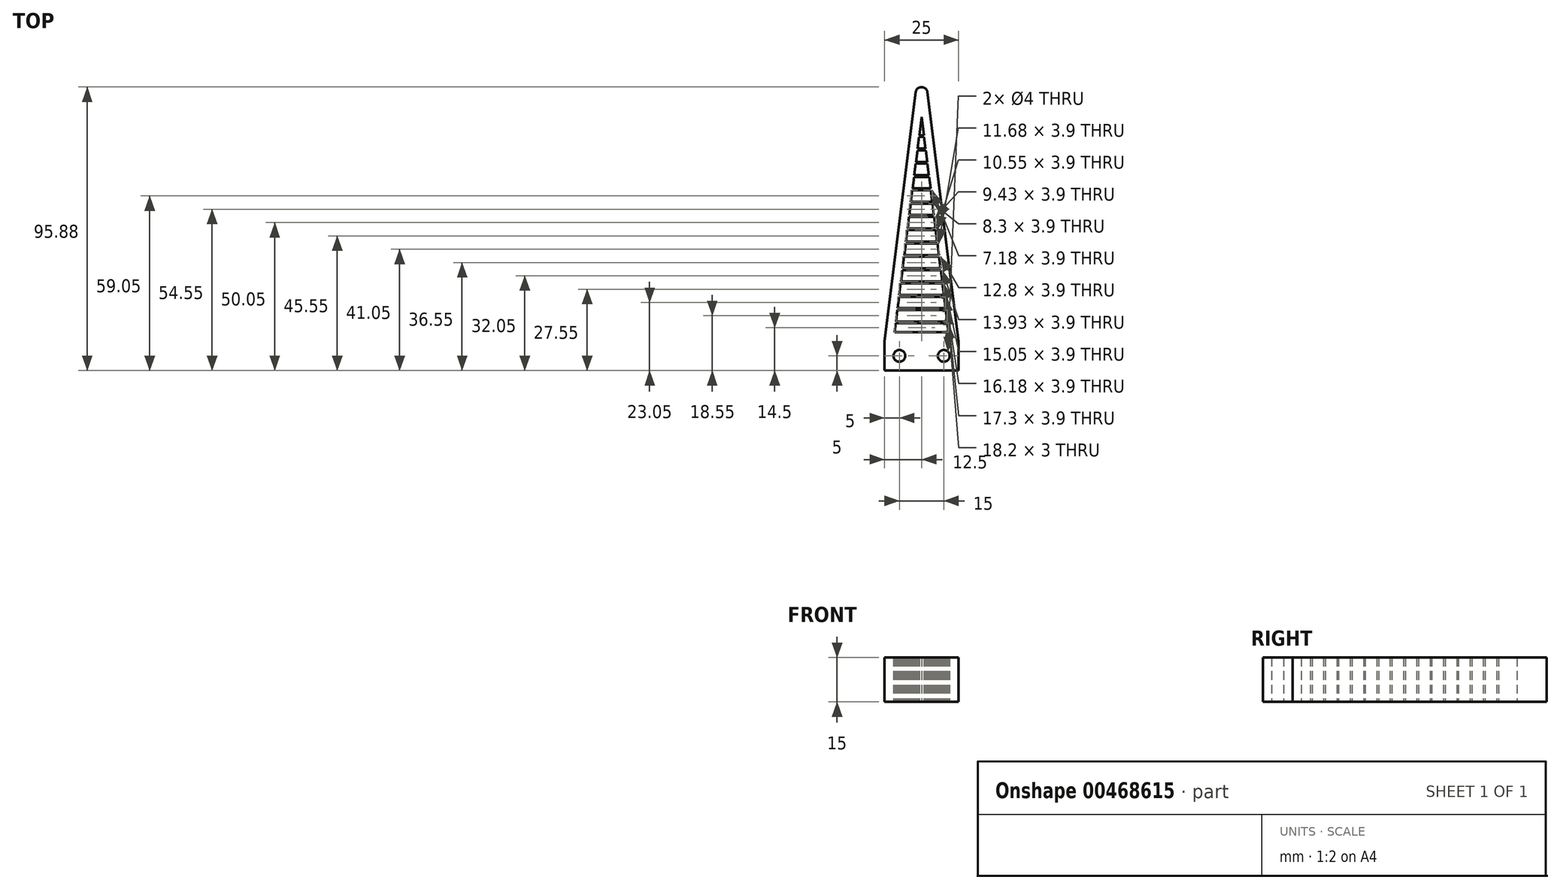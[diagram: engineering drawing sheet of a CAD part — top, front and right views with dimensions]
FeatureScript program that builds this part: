
annotation { "Feature Type Name" : "Feature", "Feature Type Description" : "" }
export const myFeature = defineFeature(function(context is Context, id is Id, definition is map)
    precondition{}
    {
        {
            var Q0;
            Q0=qCreatedBy(makeId("Top.planeOp"),FACE);
            var sketch = newSketch(context, id + "F0", { "sketchPlane" : qUnion([Q0])});
            skLineSegment(sketch, "E0", {"start": v(0, 0) * mm, "end": v(25, 0) * mm});
            skLineSegment(sketch, "E1", {"start": v(25, 0) * mm, "end": v(12.5, 100) * mm});
            skPoint(sketch, "E1.endSnap0", {"position": v(12.5, 0) * mm});
            skLineSegment(sketch, "E2", {"start": v(12.5, 100) * mm, "end": v(0, 0) * mm});
            skLineSegment(sketch, "E3.0", {"start": v(12.5, 75.81) * mm, "end": v(3.4, 3) * mm});
            skLineSegment(sketch, "E3.1", {"start": v(21.6, 3) * mm, "end": v(12.5, 75.81) * mm});
            skLineSegment(sketch, "E3.2", {"start": v(3.4, 3) * mm, "end": v(21.6, 3) * mm});
            skLineSegment(sketch, "E4", {"start": v(0, 0) * mm, "end": v(0, 100) * mm, "construction": true});
            skLineSegment(sketch, "E5", {"start": v(0, 100) * mm, "end": v(25, 100) * mm, "construction": true});
            skLineSegment(sketch, "E6", {"start": v(25, 100) * mm, "end": v(25, 0) * mm, "construction": true});
            skLineSegment(sketch, "E7.top", {"start": v(0, -10) * mm, "end": v(25, -10) * mm});
            skLineSegment(sketch, "E7.left", {"start": v(0, 0) * mm, "end": v(0, -10) * mm});
            skLineSegment(sketch, "E7.right", {"start": v(25, 0) * mm, "end": v(25, -10) * mm});
            skCircle(sketch, "E8", {"center": v(20, -5) * mm, "radius": 2 * mm});
            skPoint(sketch, "E8.centerSnap0", {"position": v(25, -5) * mm});
            skCircle(sketch, "E9", {"center": v(5, -5) * mm, "radius": 2 * mm});
            skPoint(sketch, "E9.centerSnap0", {"position": v(0, -5) * mm});
            skLineSegment(sketch, "E10", {"start": v(3.77, 6) * mm, "end": v(21.23, 6) * mm});
            skLineSegment(sketch, "E11", {"start": v(3.85, 6.6) * mm, "end": v(21.15, 6.6) * mm});
            skLineSegment(sketch, "E12.0.1.0", {"start": v(3.77, 10.5) * mm, "end": v(21.23, 10.5) * mm});
            skLineSegment(sketch, "E12.0.1.1", {"start": v(3.85, 11.1) * mm, "end": v(21.15, 11.1) * mm});
            skLineSegment(sketch, "E12.0.2.0", {"start": v(3.77, 15) * mm, "end": v(21.23, 15) * mm});
            skLineSegment(sketch, "E12.0.2.1", {"start": v(3.85, 15.6) * mm, "end": v(21.15, 15.6) * mm});
            skLineSegment(sketch, "E12.0.3.0", {"start": v(3.77, 19.5) * mm, "end": v(21.23, 19.5) * mm});
            skLineSegment(sketch, "E12.0.3.1", {"start": v(3.85, 20.1) * mm, "end": v(21.15, 20.1) * mm});
            skLineSegment(sketch, "E12.0.4.0", {"start": v(3.77, 24) * mm, "end": v(21.23, 24) * mm});
            skLineSegment(sketch, "E12.0.4.1", {"start": v(3.85, 24.6) * mm, "end": v(21.15, 24.6) * mm});
            skLineSegment(sketch, "E12.0.5.0", {"start": v(3.77, 28.5) * mm, "end": v(21.23, 28.5) * mm});
            skLineSegment(sketch, "E12.0.5.1", {"start": v(3.85, 29.1) * mm, "end": v(21.15, 29.1) * mm});
            skLineSegment(sketch, "E12.0.6.0", {"start": v(3.77, 33) * mm, "end": v(21.23, 33) * mm});
            skLineSegment(sketch, "E12.0.6.1", {"start": v(3.85, 33.6) * mm, "end": v(21.15, 33.6) * mm});
            skLineSegment(sketch, "E12.0.7.0", {"start": v(3.77, 37.5) * mm, "end": v(21.23, 37.5) * mm});
            skLineSegment(sketch, "E12.0.7.1", {"start": v(3.85, 38.1) * mm, "end": v(21.15, 38.1) * mm});
            skLineSegment(sketch, "E12.0.8.0", {"start": v(3.77, 42) * mm, "end": v(21.23, 42) * mm});
            skLineSegment(sketch, "E12.0.8.1", {"start": v(3.85, 42.6) * mm, "end": v(21.15, 42.6) * mm});
            skLineSegment(sketch, "E12.0.9.0", {"start": v(3.77, 46.5) * mm, "end": v(21.23, 46.5) * mm});
            skLineSegment(sketch, "E12.0.9.1", {"start": v(3.85, 47.1) * mm, "end": v(21.15, 47.1) * mm});
            skLineSegment(sketch, "E12.0.10.0", {"start": v(3.77, 51) * mm, "end": v(21.23, 51) * mm});
            skLineSegment(sketch, "E12.0.10.1", {"start": v(3.85, 51.6) * mm, "end": v(21.15, 51.6) * mm});
            skLineSegment(sketch, "E12.direction1", {"start": v(3.77, 6) * mm, "end": v(35.36, 6) * mm, "construction": true});
            skLineSegment(sketch, "E12.direction2", {"start": v(3.77, 6) * mm, "end": v(3.77, 10.5) * mm, "construction": true});
            skLineSegment(sketch, "E13.0.0.11", {"start": v(3.77, 55.5) * mm, "end": v(21.23, 55.5) * mm});
            skLineSegment(sketch, "E13.3.0.11", {"start": v(3.85, 56.1) * mm, "end": v(21.15, 56.1) * mm});
            skLineSegment(sketch, "E13.0.0.12", {"start": v(3.77, 60) * mm, "end": v(21.23, 60) * mm});
            skLineSegment(sketch, "E13.3.0.12", {"start": v(3.85, 60.6) * mm, "end": v(21.15, 60.6) * mm});
            skLineSegment(sketch, "E13.0.0.13", {"start": v(3.77, 64.5) * mm, "end": v(21.23, 64.5) * mm});
            skLineSegment(sketch, "E13.3.0.13", {"start": v(3.85, 65.1) * mm, "end": v(21.15, 65.1) * mm});
            skLineSegment(sketch, "E13.0.0.14", {"start": v(3.77, 69) * mm, "end": v(21.23, 69) * mm});
            skLineSegment(sketch, "E13.3.0.14", {"start": v(3.85, 69.6) * mm, "end": v(21.15, 69.6) * mm});
            skSolve(sketch);
        }
        {
            var Q0;
            {var subQ0=sQuery(id+"F0.wireOp",EDGE,"E12.0.5.0");var subQ1=sQuery(id+"F0.wireOp",EDGE,"E1");var subQ2=makeQuery(id+"F0.imprint","INTERSECT",VERTEX,{"derivedFrom":[subQ1,subQ0]});Q0=makeQuery(id+"F0.imprint","IMPRINT",FACE,{"disambiguationData":[TD([[makeQuery(id+"F0.imprint","IMPRINT",EDGE,{"disambiguationData":[TD([[subQ2,-1.0]])],"derivedFrom":subQ1}),1.0]])]});}
            var Q1;
            {var subQ0=sQuery(id+"F0.wireOp",EDGE,"E12.0.5.1");var subQ1=sQuery(id+"F0.wireOp",EDGE,"E1");var subQ2=makeQuery(id+"F0.imprint","INTERSECT",VERTEX,{"derivedFrom":[subQ1,subQ0]});Q1=makeQuery(id+"F0.imprint","IMPRINT",FACE,{"disambiguationData":[TD([[makeQuery(id+"F0.imprint","IMPRINT",EDGE,{"disambiguationData":[TD([[subQ2,-1.0]])],"derivedFrom":subQ1}),1.0]])]});}
            var Q2;
            {var subQ0=sQuery(id+"F0.wireOp",EDGE,"E12.0.6.0");var subQ1=sQuery(id+"F0.wireOp",EDGE,"E1");var subQ2=makeQuery(id+"F0.imprint","INTERSECT",VERTEX,{"derivedFrom":[subQ1,subQ0]});Q2=makeQuery(id+"F0.imprint","IMPRINT",FACE,{"disambiguationData":[TD([[makeQuery(id+"F0.imprint","IMPRINT",EDGE,{"disambiguationData":[TD([[subQ2,-1.0]])],"derivedFrom":subQ1}),1.0]])]});}
            var Q3;
            {var subQ0=sQuery(id+"F0.wireOp",EDGE,"E12.0.6.1");var subQ1=sQuery(id+"F0.wireOp",EDGE,"E1");var subQ2=makeQuery(id+"F0.imprint","INTERSECT",VERTEX,{"derivedFrom":[subQ1,subQ0]});Q3=makeQuery(id+"F0.imprint","IMPRINT",FACE,{"disambiguationData":[TD([[makeQuery(id+"F0.imprint","IMPRINT",EDGE,{"disambiguationData":[TD([[subQ2,-1.0]])],"derivedFrom":subQ1}),1.0]])]});}
            var Q4;
            {var subQ0=sQuery(id+"F0.wireOp",EDGE,"E12.0.7.0");var subQ1=sQuery(id+"F0.wireOp",EDGE,"E1");var subQ2=makeQuery(id+"F0.imprint","INTERSECT",VERTEX,{"derivedFrom":[subQ1,subQ0]});Q4=makeQuery(id+"F0.imprint","IMPRINT",FACE,{"disambiguationData":[TD([[makeQuery(id+"F0.imprint","IMPRINT",EDGE,{"disambiguationData":[TD([[subQ2,-1.0]])],"derivedFrom":subQ1}),1.0]])]});}
            var Q5;
            {var subQ0=sQuery(id+"F0.wireOp",EDGE,"E12.0.7.1");var subQ1=sQuery(id+"F0.wireOp",EDGE,"E1");var subQ2=makeQuery(id+"F0.imprint","INTERSECT",VERTEX,{"derivedFrom":[subQ1,subQ0]});Q5=makeQuery(id+"F0.imprint","IMPRINT",FACE,{"disambiguationData":[TD([[makeQuery(id+"F0.imprint","IMPRINT",EDGE,{"disambiguationData":[TD([[subQ2,-1.0]])],"derivedFrom":subQ1}),1.0]])]});}
            var Q6;
            {var subQ0=sQuery(id+"F0.wireOp",EDGE,"E12.0.8.0");var subQ1=sQuery(id+"F0.wireOp",EDGE,"E1");var subQ2=makeQuery(id+"F0.imprint","INTERSECT",VERTEX,{"derivedFrom":[subQ1,subQ0]});Q6=makeQuery(id+"F0.imprint","IMPRINT",FACE,{"disambiguationData":[TD([[makeQuery(id+"F0.imprint","IMPRINT",EDGE,{"disambiguationData":[TD([[subQ2,-1.0]])],"derivedFrom":subQ1}),1.0]])]});}
            var Q7;
            {var subQ0=sQuery(id+"F0.wireOp",EDGE,"E12.0.8.1");var subQ1=sQuery(id+"F0.wireOp",EDGE,"E1");var subQ2=makeQuery(id+"F0.imprint","INTERSECT",VERTEX,{"derivedFrom":[subQ1,subQ0]});Q7=makeQuery(id+"F0.imprint","IMPRINT",FACE,{"disambiguationData":[TD([[makeQuery(id+"F0.imprint","IMPRINT",EDGE,{"disambiguationData":[TD([[subQ2,-1.0]])],"derivedFrom":subQ1}),1.0]])]});}
            var Q8;
            {var subQ0=sQuery(id+"F0.wireOp",EDGE,"E12.0.9.0");var subQ1=sQuery(id+"F0.wireOp",EDGE,"E1");var subQ2=makeQuery(id+"F0.imprint","INTERSECT",VERTEX,{"derivedFrom":[subQ1,subQ0]});Q8=makeQuery(id+"F0.imprint","IMPRINT",FACE,{"disambiguationData":[TD([[makeQuery(id+"F0.imprint","IMPRINT",EDGE,{"disambiguationData":[TD([[subQ2,-1.0]])],"derivedFrom":subQ1}),1.0]])]});}
            var Q9;
            {var subQ0=sQuery(id+"F0.wireOp",EDGE,"E12.0.9.1");var subQ1=sQuery(id+"F0.wireOp",EDGE,"E1");var subQ2=makeQuery(id+"F0.imprint","INTERSECT",VERTEX,{"derivedFrom":[subQ1,subQ0]});Q9=makeQuery(id+"F0.imprint","IMPRINT",FACE,{"disambiguationData":[TD([[makeQuery(id+"F0.imprint","IMPRINT",EDGE,{"disambiguationData":[TD([[subQ2,-1.0]])],"derivedFrom":subQ1}),1.0]])]});}
            var Q10;
            {var subQ0=sQuery(id+"F0.wireOp",EDGE,"E12.0.10.0");var subQ1=sQuery(id+"F0.wireOp",EDGE,"E1");var subQ2=makeQuery(id+"F0.imprint","INTERSECT",VERTEX,{"derivedFrom":[subQ1,subQ0]});Q10=makeQuery(id+"F0.imprint","IMPRINT",FACE,{"disambiguationData":[TD([[makeQuery(id+"F0.imprint","IMPRINT",EDGE,{"disambiguationData":[TD([[subQ2,-1.0]])],"derivedFrom":subQ1}),1.0]])]});}
            var Q11;
            {var subQ0=sQuery(id+"F0.wireOp",EDGE,"E12.0.10.1");var subQ1=sQuery(id+"F0.wireOp",EDGE,"E1");var subQ2=makeQuery(id+"F0.imprint","INTERSECT",VERTEX,{"derivedFrom":[subQ1,subQ0]});Q11=makeQuery(id+"F0.imprint","IMPRINT",FACE,{"disambiguationData":[TD([[makeQuery(id+"F0.imprint","IMPRINT",EDGE,{"disambiguationData":[TD([[subQ2,-1.0]])],"derivedFrom":subQ1}),1.0]])]});}
            var Q12;
            {var subQ0=sQuery(id+"F0.wireOp",EDGE,"E13.0.0.11");var subQ1=sQuery(id+"F0.wireOp",EDGE,"E1");var subQ2=makeQuery(id+"F0.imprint","INTERSECT",VERTEX,{"derivedFrom":[subQ1,subQ0]});Q12=makeQuery(id+"F0.imprint","IMPRINT",FACE,{"disambiguationData":[TD([[makeQuery(id+"F0.imprint","IMPRINT",EDGE,{"disambiguationData":[TD([[subQ2,-1.0]])],"derivedFrom":subQ1}),1.0]])]});}
            var Q13;
            {var subQ0=sQuery(id+"F0.wireOp",EDGE,"E13.3.0.11");var subQ1=sQuery(id+"F0.wireOp",EDGE,"E1");var subQ2=makeQuery(id+"F0.imprint","INTERSECT",VERTEX,{"derivedFrom":[subQ1,subQ0]});Q13=makeQuery(id+"F0.imprint","IMPRINT",FACE,{"disambiguationData":[TD([[makeQuery(id+"F0.imprint","IMPRINT",EDGE,{"disambiguationData":[TD([[subQ2,-1.0]])],"derivedFrom":subQ1}),1.0]])]});}
            var Q14;
            {var subQ0=sQuery(id+"F0.wireOp",EDGE,"E13.0.0.12");var subQ1=sQuery(id+"F0.wireOp",EDGE,"E1");var subQ2=makeQuery(id+"F0.imprint","INTERSECT",VERTEX,{"derivedFrom":[subQ1,subQ0]});Q14=makeQuery(id+"F0.imprint","IMPRINT",FACE,{"disambiguationData":[TD([[makeQuery(id+"F0.imprint","IMPRINT",EDGE,{"disambiguationData":[TD([[subQ2,-1.0]])],"derivedFrom":subQ1}),1.0]])]});}
            var Q15;
            {var subQ0=sQuery(id+"F0.wireOp",EDGE,"E13.3.0.12");var subQ1=sQuery(id+"F0.wireOp",EDGE,"E1");var subQ2=makeQuery(id+"F0.imprint","INTERSECT",VERTEX,{"derivedFrom":[subQ1,subQ0]});Q15=makeQuery(id+"F0.imprint","IMPRINT",FACE,{"disambiguationData":[TD([[makeQuery(id+"F0.imprint","IMPRINT",EDGE,{"disambiguationData":[TD([[subQ2,-1.0]])],"derivedFrom":subQ1}),1.0]])]});}
            var Q16;
            {var subQ0=sQuery(id+"F0.wireOp",EDGE,"E13.0.0.13");var subQ1=sQuery(id+"F0.wireOp",EDGE,"E1");var subQ2=makeQuery(id+"F0.imprint","INTERSECT",VERTEX,{"derivedFrom":[subQ1,subQ0]});Q16=makeQuery(id+"F0.imprint","IMPRINT",FACE,{"disambiguationData":[TD([[makeQuery(id+"F0.imprint","IMPRINT",EDGE,{"disambiguationData":[TD([[subQ2,-1.0]])],"derivedFrom":subQ1}),1.0]])]});}
            var Q17;
            {var subQ0=sQuery(id+"F0.wireOp",EDGE,"E13.3.0.13");var subQ1=sQuery(id+"F0.wireOp",EDGE,"E1");var subQ2=makeQuery(id+"F0.imprint","INTERSECT",VERTEX,{"derivedFrom":[subQ1,subQ0]});Q17=makeQuery(id+"F0.imprint","IMPRINT",FACE,{"disambiguationData":[TD([[makeQuery(id+"F0.imprint","IMPRINT",EDGE,{"disambiguationData":[TD([[subQ2,-1.0]])],"derivedFrom":subQ1}),1.0]])]});}
            var Q18;
            {var subQ0=sQuery(id+"F0.wireOp",EDGE,"E13.0.0.14");var subQ1=sQuery(id+"F0.wireOp",EDGE,"E1");var subQ2=makeQuery(id+"F0.imprint","INTERSECT",VERTEX,{"derivedFrom":[subQ1,subQ0]});Q18=makeQuery(id+"F0.imprint","IMPRINT",FACE,{"disambiguationData":[TD([[makeQuery(id+"F0.imprint","IMPRINT",EDGE,{"disambiguationData":[TD([[subQ2,-1.0]])],"derivedFrom":subQ1}),1.0]])]});}
            var Q19;
            {var subQ0=sQuery(id+"F0.wireOp",EDGE,"E13.3.0.14");var subQ1=sQuery(id+"F0.wireOp",EDGE,"E1");var subQ2=makeQuery(id+"F0.imprint","INTERSECT",VERTEX,{"derivedFrom":[subQ1,subQ0]});Q19=makeQuery(id+"F0.imprint","IMPRINT",FACE,{"disambiguationData":[TD([[makeQuery(id+"F0.imprint","IMPRINT",EDGE,{"disambiguationData":[TD([[subQ2,-1.0]])],"derivedFrom":subQ1}),1.0]])]});}
            var Q20;
            {var subQ0=sQuery(id+"F0.wireOp",EDGE,"988712d8-d478-4dcb-9f80-e58582f5ab0d.0.0.15");var subQ1=sQuery(id+"F0.wireOp",EDGE,"E1");var subQ2=makeQuery(id+"F0.imprint","INTERSECT",VERTEX,{"derivedFrom":[subQ1,subQ0]});Q20=makeQuery(id+"F0.imprint","IMPRINT",FACE,{"disambiguationData":[TD([[makeQuery(id+"F0.imprint","IMPRINT",EDGE,{"disambiguationData":[TD([[subQ2,-1.0]])],"derivedFrom":subQ1}),1.0]])]});}
            var Q21;
            Q21=makeQuery(id+"F0.imprint","IMPRINT",FACE,{"disambiguationData":[TD([[makeQuery(id+"F0.imprint","IMPRINT",EDGE,{"derivedFrom":sQuery(id+"F0.wireOp",EDGE,"E0")}),-1.0]])]});
            var Q22;
            {var subQ5=sQuery(id+"F0.wireOp",EDGE,"E2");var subQ6=sQuery(id+"F0.wireOp",EDGE,"E1");var subQ7=makeQuery(id+"F0.imprint","INTERSECT",VERTEX,{"derivedFrom":[subQ6,subQ5]});Q22=makeQuery(id+"F0.imprint","IMPRINT",FACE,{"disambiguationData":[TD([[makeQuery(id+"F0.imprint","IMPRINT",EDGE,{"disambiguationData":[TD([[subQ7,1.0]])],"derivedFrom":subQ6}),1.0]])]});}
            var Q23;
            {var subQ0=sQuery(id+"F0.wireOp",EDGE,"E13.0.0.13");var subQ1=sQuery(id+"F0.wireOp",EDGE,"E2");var subQ2=makeQuery(id+"F0.imprint","INTERSECT",VERTEX,{"derivedFrom":[subQ1,subQ0]});Q23=makeQuery(id+"F0.imprint","IMPRINT",FACE,{"disambiguationData":[TD([[makeQuery(id+"F0.imprint","IMPRINT",EDGE,{"disambiguationData":[TD([[subQ2,-1.0]])],"derivedFrom":subQ1}),1.0]])]});}
            var Q24;
            {var subQ0=sQuery(id+"F0.wireOp",EDGE,"E13.3.0.14");var subQ1=sQuery(id+"F0.wireOp",EDGE,"E2");var subQ2=makeQuery(id+"F0.imprint","INTERSECT",VERTEX,{"derivedFrom":[subQ1,subQ0]});Q24=makeQuery(id+"F0.imprint","IMPRINT",FACE,{"disambiguationData":[TD([[makeQuery(id+"F0.imprint","IMPRINT",EDGE,{"disambiguationData":[TD([[subQ2,-1.0]])],"derivedFrom":subQ1}),1.0]])]});}
            var Q25;
            {var subQ0=sQuery(id+"F0.wireOp",EDGE,"E13.3.0.13");var subQ1=sQuery(id+"F0.wireOp",EDGE,"E2");var subQ2=makeQuery(id+"F0.imprint","INTERSECT",VERTEX,{"derivedFrom":[subQ1,subQ0]});Q25=makeQuery(id+"F0.imprint","IMPRINT",FACE,{"disambiguationData":[TD([[makeQuery(id+"F0.imprint","IMPRINT",EDGE,{"disambiguationData":[TD([[subQ2,-1.0]])],"derivedFrom":subQ1}),1.0]])]});}
            var Q26;
            {var subQ0=sQuery(id+"F0.wireOp",EDGE,"988712d8-d478-4dcb-9f80-e58582f5ab0d.0.0.15");var subQ1=sQuery(id+"F0.wireOp",EDGE,"E2");var subQ2=makeQuery(id+"F0.imprint","INTERSECT",VERTEX,{"derivedFrom":[subQ1,subQ0]});Q26=makeQuery(id+"F0.imprint","IMPRINT",FACE,{"disambiguationData":[TD([[makeQuery(id+"F0.imprint","IMPRINT",EDGE,{"disambiguationData":[TD([[subQ2,-1.0]])],"derivedFrom":subQ1}),1.0]])]});}
            var Q27;
            {var subQ0=sQuery(id+"F0.wireOp",EDGE,"E13.0.0.14");var subQ1=sQuery(id+"F0.wireOp",EDGE,"E2");var subQ2=makeQuery(id+"F0.imprint","INTERSECT",VERTEX,{"derivedFrom":[subQ1,subQ0]});Q27=makeQuery(id+"F0.imprint","IMPRINT",FACE,{"disambiguationData":[TD([[makeQuery(id+"F0.imprint","IMPRINT",EDGE,{"disambiguationData":[TD([[subQ2,-1.0]])],"derivedFrom":subQ1}),1.0]])]});}
            var Q28;
            {var subQ0=sQuery(id+"F0.wireOp",EDGE,"988712d8-d478-4dcb-9f80-e58582f5ab0d.3.0.15");var subQ1=sQuery(id+"F0.wireOp",EDGE,"E2");var subQ2=makeQuery(id+"F0.imprint","INTERSECT",VERTEX,{"derivedFrom":[subQ1,subQ0]});Q28=makeQuery(id+"F0.imprint","IMPRINT",FACE,{"disambiguationData":[TD([[makeQuery(id+"F0.imprint","IMPRINT",EDGE,{"disambiguationData":[TD([[subQ2,-1.0]])],"derivedFrom":subQ1}),1.0]])]});}
            var Q29;
            {var subQ0=sQuery(id+"F0.wireOp",EDGE,"E12.0.10.0");var subQ1=sQuery(id+"F0.wireOp",EDGE,"E2");var subQ2=makeQuery(id+"F0.imprint","INTERSECT",VERTEX,{"derivedFrom":[subQ1,subQ0]});Q29=makeQuery(id+"F0.imprint","IMPRINT",FACE,{"disambiguationData":[TD([[makeQuery(id+"F0.imprint","IMPRINT",EDGE,{"disambiguationData":[TD([[subQ2,-1.0]])],"derivedFrom":subQ1}),1.0]])]});}
            var Q30;
            {var subQ0=sQuery(id+"F0.wireOp",EDGE,"E13.0.0.12");var subQ1=sQuery(id+"F0.wireOp",EDGE,"E2");var subQ2=makeQuery(id+"F0.imprint","INTERSECT",VERTEX,{"derivedFrom":[subQ1,subQ0]});Q30=makeQuery(id+"F0.imprint","IMPRINT",FACE,{"disambiguationData":[TD([[makeQuery(id+"F0.imprint","IMPRINT",EDGE,{"disambiguationData":[TD([[subQ2,-1.0]])],"derivedFrom":subQ1}),1.0]])]});}
            var Q31;
            {var subQ0=sQuery(id+"F0.wireOp",EDGE,"E13.3.0.11");var subQ1=sQuery(id+"F0.wireOp",EDGE,"E2");var subQ2=makeQuery(id+"F0.imprint","INTERSECT",VERTEX,{"derivedFrom":[subQ1,subQ0]});Q31=makeQuery(id+"F0.imprint","IMPRINT",FACE,{"disambiguationData":[TD([[makeQuery(id+"F0.imprint","IMPRINT",EDGE,{"disambiguationData":[TD([[subQ2,-1.0]])],"derivedFrom":subQ1}),1.0]])]});}
            var Q32;
            {var subQ0=sQuery(id+"F0.wireOp",EDGE,"E13.3.0.12");var subQ1=sQuery(id+"F0.wireOp",EDGE,"E2");var subQ2=makeQuery(id+"F0.imprint","INTERSECT",VERTEX,{"derivedFrom":[subQ1,subQ0]});Q32=makeQuery(id+"F0.imprint","IMPRINT",FACE,{"disambiguationData":[TD([[makeQuery(id+"F0.imprint","IMPRINT",EDGE,{"disambiguationData":[TD([[subQ2,-1.0]])],"derivedFrom":subQ1}),1.0]])]});}
            var Q33;
            {var subQ0=sQuery(id+"F0.wireOp",EDGE,"E12.0.10.1");var subQ1=sQuery(id+"F0.wireOp",EDGE,"E2");var subQ2=makeQuery(id+"F0.imprint","INTERSECT",VERTEX,{"derivedFrom":[subQ1,subQ0]});Q33=makeQuery(id+"F0.imprint","IMPRINT",FACE,{"disambiguationData":[TD([[makeQuery(id+"F0.imprint","IMPRINT",EDGE,{"disambiguationData":[TD([[subQ2,-1.0]])],"derivedFrom":subQ1}),1.0]])]});}
            var Q34;
            {var subQ0=sQuery(id+"F0.wireOp",EDGE,"E13.0.0.11");var subQ1=sQuery(id+"F0.wireOp",EDGE,"E2");var subQ2=makeQuery(id+"F0.imprint","INTERSECT",VERTEX,{"derivedFrom":[subQ1,subQ0]});Q34=makeQuery(id+"F0.imprint","IMPRINT",FACE,{"disambiguationData":[TD([[makeQuery(id+"F0.imprint","IMPRINT",EDGE,{"disambiguationData":[TD([[subQ2,-1.0]])],"derivedFrom":subQ1}),1.0]])]});}
            var Q35;
            {var subQ0=sQuery(id+"F0.wireOp",EDGE,"E12.0.8.0");var subQ1=sQuery(id+"F0.wireOp",EDGE,"E2");var subQ2=makeQuery(id+"F0.imprint","INTERSECT",VERTEX,{"derivedFrom":[subQ1,subQ0]});Q35=makeQuery(id+"F0.imprint","IMPRINT",FACE,{"disambiguationData":[TD([[makeQuery(id+"F0.imprint","IMPRINT",EDGE,{"disambiguationData":[TD([[subQ2,-1.0]])],"derivedFrom":subQ1}),1.0]])]});}
            var Q36;
            {var subQ0=sQuery(id+"F0.wireOp",EDGE,"E12.0.6.1");var subQ1=sQuery(id+"F0.wireOp",EDGE,"E2");var subQ2=makeQuery(id+"F0.imprint","INTERSECT",VERTEX,{"derivedFrom":[subQ1,subQ0]});Q36=makeQuery(id+"F0.imprint","IMPRINT",FACE,{"disambiguationData":[TD([[makeQuery(id+"F0.imprint","IMPRINT",EDGE,{"disambiguationData":[TD([[subQ2,-1.0]])],"derivedFrom":subQ1}),1.0]])]});}
            var Q37;
            {var subQ0=sQuery(id+"F0.wireOp",EDGE,"E12.0.8.1");var subQ1=sQuery(id+"F0.wireOp",EDGE,"E2");var subQ2=makeQuery(id+"F0.imprint","INTERSECT",VERTEX,{"derivedFrom":[subQ1,subQ0]});Q37=makeQuery(id+"F0.imprint","IMPRINT",FACE,{"disambiguationData":[TD([[makeQuery(id+"F0.imprint","IMPRINT",EDGE,{"disambiguationData":[TD([[subQ2,-1.0]])],"derivedFrom":subQ1}),1.0]])]});}
            var Q38;
            {var subQ0=sQuery(id+"F0.wireOp",EDGE,"E12.0.9.0");var subQ1=sQuery(id+"F0.wireOp",EDGE,"E2");var subQ2=makeQuery(id+"F0.imprint","INTERSECT",VERTEX,{"derivedFrom":[subQ1,subQ0]});Q38=makeQuery(id+"F0.imprint","IMPRINT",FACE,{"disambiguationData":[TD([[makeQuery(id+"F0.imprint","IMPRINT",EDGE,{"disambiguationData":[TD([[subQ2,-1.0]])],"derivedFrom":subQ1}),1.0]])]});}
            var Q39;
            {var subQ0=sQuery(id+"F0.wireOp",EDGE,"E12.0.7.0");var subQ1=sQuery(id+"F0.wireOp",EDGE,"E2");var subQ2=makeQuery(id+"F0.imprint","INTERSECT",VERTEX,{"derivedFrom":[subQ1,subQ0]});Q39=makeQuery(id+"F0.imprint","IMPRINT",FACE,{"disambiguationData":[TD([[makeQuery(id+"F0.imprint","IMPRINT",EDGE,{"disambiguationData":[TD([[subQ2,-1.0]])],"derivedFrom":subQ1}),1.0]])]});}
            var Q40;
            {var subQ0=sQuery(id+"F0.wireOp",EDGE,"E12.0.6.0");var subQ1=sQuery(id+"F0.wireOp",EDGE,"E2");var subQ2=makeQuery(id+"F0.imprint","INTERSECT",VERTEX,{"derivedFrom":[subQ1,subQ0]});Q40=makeQuery(id+"F0.imprint","IMPRINT",FACE,{"disambiguationData":[TD([[makeQuery(id+"F0.imprint","IMPRINT",EDGE,{"disambiguationData":[TD([[subQ2,-1.0]])],"derivedFrom":subQ1}),1.0]])]});}
            var Q41;
            {var subQ0=sQuery(id+"F0.wireOp",EDGE,"E12.0.9.1");var subQ1=sQuery(id+"F0.wireOp",EDGE,"E2");var subQ2=makeQuery(id+"F0.imprint","INTERSECT",VERTEX,{"derivedFrom":[subQ1,subQ0]});Q41=makeQuery(id+"F0.imprint","IMPRINT",FACE,{"disambiguationData":[TD([[makeQuery(id+"F0.imprint","IMPRINT",EDGE,{"disambiguationData":[TD([[subQ2,-1.0]])],"derivedFrom":subQ1}),1.0]])]});}
            var Q42;
            {var subQ0=sQuery(id+"F0.wireOp",EDGE,"E12.0.7.1");var subQ1=sQuery(id+"F0.wireOp",EDGE,"E2");var subQ2=makeQuery(id+"F0.imprint","INTERSECT",VERTEX,{"derivedFrom":[subQ1,subQ0]});Q42=makeQuery(id+"F0.imprint","IMPRINT",FACE,{"disambiguationData":[TD([[makeQuery(id+"F0.imprint","IMPRINT",EDGE,{"disambiguationData":[TD([[subQ2,-1.0]])],"derivedFrom":subQ1}),1.0]])]});}
            var Q43;
            {var subQ27=sQuery(id+"F0.wireOp",EDGE,"E3.2");Q43=makeQuery(id+"F0.imprint","IMPRINT",FACE,{"disambiguationData":[TD([[makeQuery(id+"F0.imprint","IMPRINT",EDGE,{"derivedFrom":subQ27}),-1.0]])]});}
            var Q44;
            {var subQ0=sQuery(id+"F0.wireOp",EDGE,"E12.0.5.1");var subQ1=sQuery(id+"F0.wireOp",EDGE,"E2");var subQ2=makeQuery(id+"F0.imprint","INTERSECT",VERTEX,{"derivedFrom":[subQ1,subQ0]});Q44=makeQuery(id+"F0.imprint","IMPRINT",FACE,{"disambiguationData":[TD([[makeQuery(id+"F0.imprint","IMPRINT",EDGE,{"disambiguationData":[TD([[subQ2,-1.0]])],"derivedFrom":subQ1}),1.0]])]});}
            var Q45;
            {var subQ0=sQuery(id+"F0.wireOp",EDGE,"E10");Q45=makeQuery(id+"F0.imprint","IMPRINT",FACE,{"disambiguationData":[TD([[makeQuery(id+"F0.imprint","IMPRINT",EDGE,{"derivedFrom":subQ0}),1.0]])]});}
            var Q46;
            {var subQ0=sQuery(id+"F0.wireOp",EDGE,"E12.0.1.1");var subQ1=sQuery(id+"F0.wireOp",EDGE,"E3.0");var subQ2=makeQuery(id+"F0.imprint","INTERSECT",VERTEX,{"derivedFrom":[subQ1,subQ0]});Q46=makeQuery(id+"F0.imprint","IMPRINT",FACE,{"disambiguationData":[TD([[makeQuery(id+"F0.imprint","IMPRINT",EDGE,{"disambiguationData":[TD([[subQ2,-1.0]])],"derivedFrom":subQ1}),1.0]])]});}
            var Q47;
            {var subQ0=sQuery(id+"F0.wireOp",EDGE,"E12.0.2.1");var subQ1=sQuery(id+"F0.wireOp",EDGE,"E3.0");var subQ2=makeQuery(id+"F0.imprint","INTERSECT",VERTEX,{"derivedFrom":[subQ1,subQ0]});Q47=makeQuery(id+"F0.imprint","IMPRINT",FACE,{"disambiguationData":[TD([[makeQuery(id+"F0.imprint","IMPRINT",EDGE,{"disambiguationData":[TD([[subQ2,-1.0]])],"derivedFrom":subQ1}),1.0]])]});}
            var Q48;
            {var subQ0=sQuery(id+"F0.wireOp",EDGE,"E12.0.3.1");var subQ1=sQuery(id+"F0.wireOp",EDGE,"E3.0");var subQ2=makeQuery(id+"F0.imprint","INTERSECT",VERTEX,{"derivedFrom":[subQ1,subQ0]});Q48=makeQuery(id+"F0.imprint","IMPRINT",FACE,{"disambiguationData":[TD([[makeQuery(id+"F0.imprint","IMPRINT",EDGE,{"disambiguationData":[TD([[subQ2,-1.0]])],"derivedFrom":subQ1}),1.0]])]});}
            var Q49;
            {var subQ0=sQuery(id+"F0.wireOp",EDGE,"E12.0.4.1");var subQ1=sQuery(id+"F0.wireOp",EDGE,"E3.0");var subQ2=makeQuery(id+"F0.imprint","INTERSECT",VERTEX,{"derivedFrom":[subQ1,subQ0]});Q49=makeQuery(id+"F0.imprint","IMPRINT",FACE,{"disambiguationData":[TD([[makeQuery(id+"F0.imprint","IMPRINT",EDGE,{"disambiguationData":[TD([[subQ2,-1.0]])],"derivedFrom":subQ1}),1.0]])]});}
            var Q50;
            {var subQ0=sQuery(id+"F0.wireOp",EDGE,"E12.0.5.1");var subQ1=sQuery(id+"F0.wireOp",EDGE,"E3.0");var subQ2=makeQuery(id+"F0.imprint","INTERSECT",VERTEX,{"derivedFrom":[subQ1,subQ0]});Q50=makeQuery(id+"F0.imprint","IMPRINT",FACE,{"disambiguationData":[TD([[makeQuery(id+"F0.imprint","IMPRINT",EDGE,{"disambiguationData":[TD([[subQ2,-1.0]])],"derivedFrom":subQ1}),1.0]])]});}
            var Q51;
            {var subQ0=sQuery(id+"F0.wireOp",EDGE,"E12.0.6.1");var subQ1=sQuery(id+"F0.wireOp",EDGE,"E3.0");var subQ2=makeQuery(id+"F0.imprint","INTERSECT",VERTEX,{"derivedFrom":[subQ1,subQ0]});Q51=makeQuery(id+"F0.imprint","IMPRINT",FACE,{"disambiguationData":[TD([[makeQuery(id+"F0.imprint","IMPRINT",EDGE,{"disambiguationData":[TD([[subQ2,-1.0]])],"derivedFrom":subQ1}),1.0]])]});}
            var Q52;
            {var subQ0=sQuery(id+"F0.wireOp",EDGE,"E12.0.7.1");var subQ1=sQuery(id+"F0.wireOp",EDGE,"E3.0");var subQ2=makeQuery(id+"F0.imprint","INTERSECT",VERTEX,{"derivedFrom":[subQ1,subQ0]});Q52=makeQuery(id+"F0.imprint","IMPRINT",FACE,{"disambiguationData":[TD([[makeQuery(id+"F0.imprint","IMPRINT",EDGE,{"disambiguationData":[TD([[subQ2,-1.0]])],"derivedFrom":subQ1}),1.0]])]});}
            var Q53;
            {var subQ0=sQuery(id+"F0.wireOp",EDGE,"E12.0.8.1");var subQ1=sQuery(id+"F0.wireOp",EDGE,"E3.0");var subQ2=makeQuery(id+"F0.imprint","INTERSECT",VERTEX,{"derivedFrom":[subQ1,subQ0]});Q53=makeQuery(id+"F0.imprint","IMPRINT",FACE,{"disambiguationData":[TD([[makeQuery(id+"F0.imprint","IMPRINT",EDGE,{"disambiguationData":[TD([[subQ2,-1.0]])],"derivedFrom":subQ1}),1.0]])]});}
            var Q54;
            {var subQ0=sQuery(id+"F0.wireOp",EDGE,"E12.0.9.1");var subQ1=sQuery(id+"F0.wireOp",EDGE,"E3.0");var subQ2=makeQuery(id+"F0.imprint","INTERSECT",VERTEX,{"derivedFrom":[subQ1,subQ0]});Q54=makeQuery(id+"F0.imprint","IMPRINT",FACE,{"disambiguationData":[TD([[makeQuery(id+"F0.imprint","IMPRINT",EDGE,{"disambiguationData":[TD([[subQ2,-1.0]])],"derivedFrom":subQ1}),1.0]])]});}
            var Q55;
            {var subQ0=sQuery(id+"F0.wireOp",EDGE,"E12.0.10.1");var subQ1=sQuery(id+"F0.wireOp",EDGE,"E3.0");var subQ2=makeQuery(id+"F0.imprint","INTERSECT",VERTEX,{"derivedFrom":[subQ1,subQ0]});Q55=makeQuery(id+"F0.imprint","IMPRINT",FACE,{"disambiguationData":[TD([[makeQuery(id+"F0.imprint","IMPRINT",EDGE,{"disambiguationData":[TD([[subQ2,-1.0]])],"derivedFrom":subQ1}),1.0]])]});}
            var Q56;
            {var subQ0=sQuery(id+"F0.wireOp",EDGE,"E13.3.0.11");var subQ1=sQuery(id+"F0.wireOp",EDGE,"E3.0");var subQ2=makeQuery(id+"F0.imprint","INTERSECT",VERTEX,{"derivedFrom":[subQ1,subQ0]});Q56=makeQuery(id+"F0.imprint","IMPRINT",FACE,{"disambiguationData":[TD([[makeQuery(id+"F0.imprint","IMPRINT",EDGE,{"disambiguationData":[TD([[subQ2,-1.0]])],"derivedFrom":subQ1}),1.0]])]});}
            var Q57;
            {var subQ0=sQuery(id+"F0.wireOp",EDGE,"E13.3.0.12");var subQ1=sQuery(id+"F0.wireOp",EDGE,"E3.0");var subQ2=makeQuery(id+"F0.imprint","INTERSECT",VERTEX,{"derivedFrom":[subQ1,subQ0]});Q57=makeQuery(id+"F0.imprint","IMPRINT",FACE,{"disambiguationData":[TD([[makeQuery(id+"F0.imprint","IMPRINT",EDGE,{"disambiguationData":[TD([[subQ2,-1.0]])],"derivedFrom":subQ1}),1.0]])]});}
            var Q58;
            {var subQ0=sQuery(id+"F0.wireOp",EDGE,"E13.3.0.13");var subQ1=sQuery(id+"F0.wireOp",EDGE,"E3.0");var subQ2=makeQuery(id+"F0.imprint","INTERSECT",VERTEX,{"derivedFrom":[subQ1,subQ0]});Q58=makeQuery(id+"F0.imprint","IMPRINT",FACE,{"disambiguationData":[TD([[makeQuery(id+"F0.imprint","IMPRINT",EDGE,{"disambiguationData":[TD([[subQ2,-1.0]])],"derivedFrom":subQ1}),1.0]])]});}
            var Q59;
            {var subQ0=sQuery(id+"F0.wireOp",EDGE,"E13.3.0.14");var subQ1=sQuery(id+"F0.wireOp",EDGE,"E3.0");var subQ2=makeQuery(id+"F0.imprint","INTERSECT",VERTEX,{"derivedFrom":[subQ1,subQ0]});Q59=makeQuery(id+"F0.imprint","IMPRINT",FACE,{"disambiguationData":[TD([[makeQuery(id+"F0.imprint","IMPRINT",EDGE,{"disambiguationData":[TD([[subQ2,-1.0]])],"derivedFrom":subQ1}),1.0]])]});}
            extrude(context, id + "F1", {"entities" : qUnion([Q0, Q1, Q2, Q3, Q4, Q5, Q6, Q7, Q8, Q9, Q10, Q11, Q12, Q13, Q14, Q15, Q16, Q17, Q18, Q19, Q20, Q21, Q22, Q23, Q24, Q25, Q26, Q27, Q28, Q29, Q30, Q31, Q32, Q33, Q34, Q35, Q36, Q37, Q38, Q39, Q40, Q41, Q42, Q43, Q44, Q45, Q46, Q47, Q48, Q49, Q50, Q51, Q52, Q53, Q54, Q55, Q56, Q57, Q58, Q59]), "depth" : 15 * mm, "symmetric" : true});
        }
        {
            var Q0;
            Q0=makeQuery(id+"F1.opExtrude","SWEPT_EDGE",EDGE,{"disambiguationData":[OSD([sQuery(id+"F0.wireOp",EDGE,"E1"),sQuery(id+"F0.wireOp",EDGE,"E2")])]});
            fillet(context, id + "F2", {"entities" : qUnion([Q0]), "radius" : 2 * mm, "tangentPropagation" : true, "allowEdgeOverflow" : false});
        }
    });
